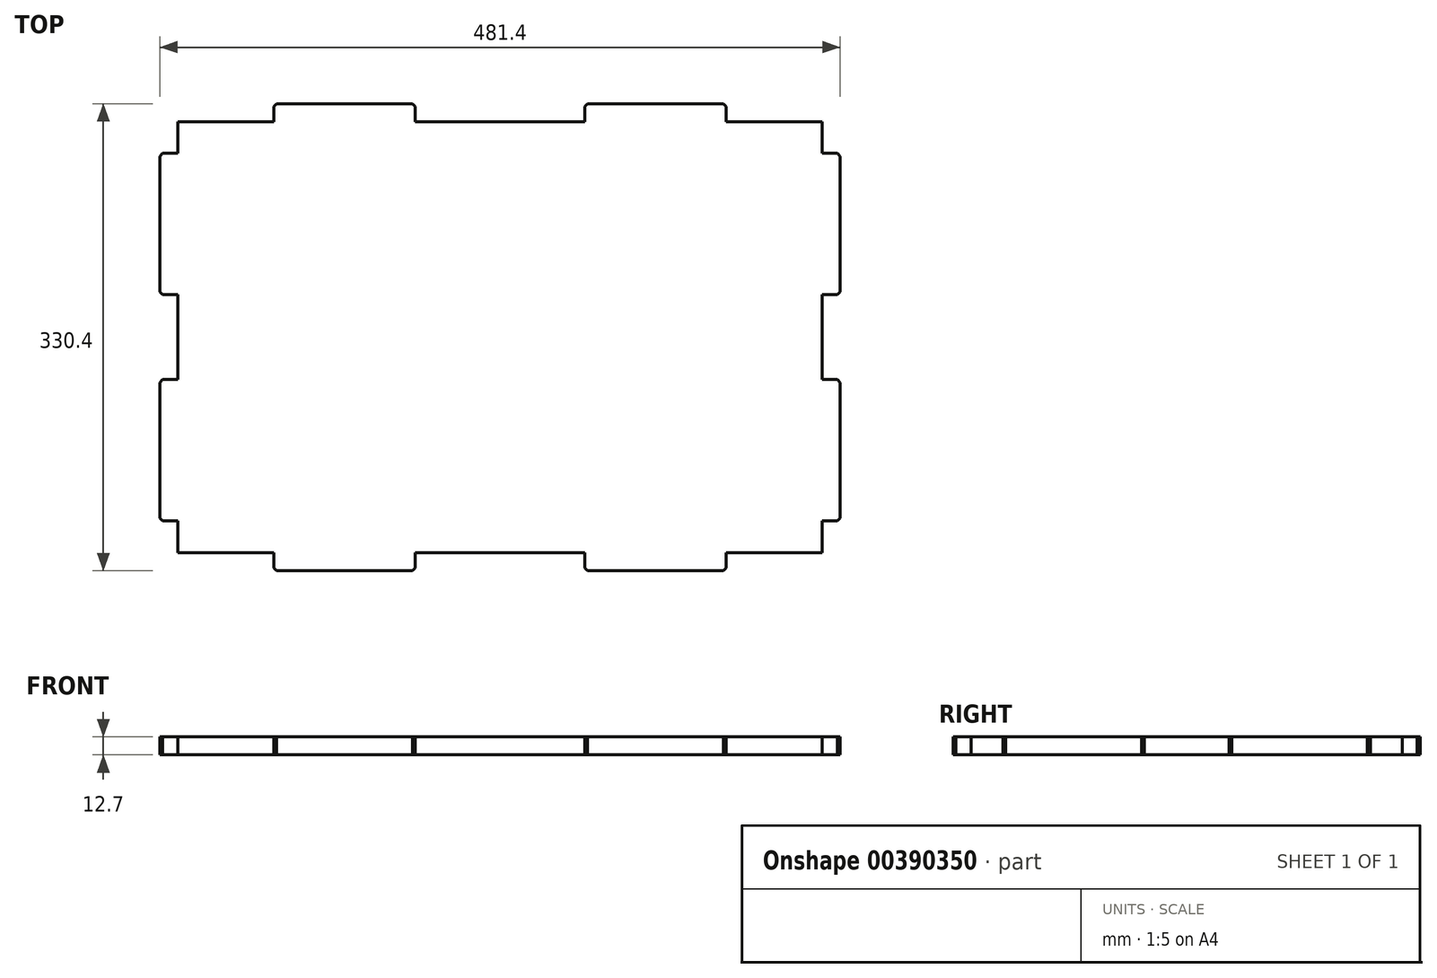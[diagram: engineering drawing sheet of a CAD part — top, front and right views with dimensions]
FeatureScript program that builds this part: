
annotation { "Feature Type Name" : "Feature", "Feature Type Description" : "" }
export const myFeature = defineFeature(function(context is Context, id is Id, definition is map)
    precondition{}
    {
        {
            var Q0;
            Q0=qCreatedBy(makeId("Top.planeOp"),FACE);
            var sketch = newSketch(context, id + "F0", { "sketchPlane" : qUnion([Q0])});
            skLineSegment(sketch, "E0.bottom", {"start": v(228, -152.5) * mm, "end": v(160, -152.5) * mm});
            skLineSegment(sketch, "E0.top", {"start": v(228, 152.5) * mm, "end": v(160, 152.5) * mm});
            skLineSegment(sketch, "E0.left", {"start": v(228, -152.5) * mm, "end": v(228, -130) * mm});
            skLineSegment(sketch, "E0.right", {"start": v(-228, -152.5) * mm, "end": v(-228, -130) * mm});
            skPoint(sketch, "E0.middle", {"position": v(0, 0) * mm});
            skLineSegment(sketch, "E1.bottom", {"start": v(-228, -30) * mm, "end": v(-240.7, -30) * mm});
            skLineSegment(sketch, "E1.top", {"start": v(-228, -130) * mm, "end": v(-240.7, -130) * mm});
            skLineSegment(sketch, "E1.right", {"start": v(-240.7, -30) * mm, "end": v(-240.7, -130) * mm});
            skLineSegment(sketch, "E2.trimOffspring", {"start": v(-228, -30) * mm, "end": v(-228, 30) * mm});
            skLineSegment(sketch, "E3.MirrorCS", {"start": v(-228, 30) * mm, "end": v(-240.7, 30) * mm});
            skLineSegment(sketch, "E4.MirrorCS", {"start": v(-228, 130) * mm, "end": v(-240.7, 130) * mm});
            skLineSegment(sketch, "E5.MirrorCS", {"start": v(-240.7, 30) * mm, "end": v(-240.7, 130) * mm});
            skLineSegment(sketch, "E6.MirrorCS", {"start": v(228, 130) * mm, "end": v(240.7, 130) * mm});
            skLineSegment(sketch, "E7.MirrorCS", {"start": v(240.7, 30) * mm, "end": v(240.7, 130) * mm});
            skLineSegment(sketch, "E8.MirrorCS", {"start": v(228, 30) * mm, "end": v(240.7, 30) * mm});
            skLineSegment(sketch, "E9.MirrorCS", {"start": v(228, -30) * mm, "end": v(240.7, -30) * mm});
            skLineSegment(sketch, "E10.MirrorCS", {"start": v(240.7, -30) * mm, "end": v(240.7, -130) * mm});
            skLineSegment(sketch, "E11.MirrorCS", {"start": v(228, -130) * mm, "end": v(240.7, -130) * mm});
            skLineSegment(sketch, "E12.trimOffspring", {"start": v(-228, 130) * mm, "end": v(-228, 152.5) * mm});
            skLineSegment(sketch, "E13.trimOffspring", {"start": v(228, 130) * mm, "end": v(228, 152.5) * mm});
            skLineSegment(sketch, "E14.trimOffspring", {"start": v(228, -30) * mm, "end": v(228, 30) * mm});
            skLineSegment(sketch, "E15.top", {"start": v(-160, 165.2) * mm, "end": v(-60, 165.2) * mm});
            skLineSegment(sketch, "E15.left", {"start": v(-160, 152.5) * mm, "end": v(-160, 165.2) * mm});
            skLineSegment(sketch, "E15.right", {"start": v(-60, 152.5) * mm, "end": v(-60, 165.2) * mm});
            skLineSegment(sketch, "E16.trimOffspring", {"start": v(-160, 152.5) * mm, "end": v(-228, 152.5) * mm});
            skLineSegment(sketch, "E17.MirrorCS", {"start": v(-60, -152.5) * mm, "end": v(-60, -165.2) * mm});
            skLineSegment(sketch, "E18.MirrorCS", {"start": v(-160, -152.5) * mm, "end": v(-160, -165.2) * mm});
            skLineSegment(sketch, "E19.MirrorCS", {"start": v(-160, -165.2) * mm, "end": v(-60, -165.2) * mm});
            skLineSegment(sketch, "E20.MirrorCS", {"start": v(160, 152.5) * mm, "end": v(160, 165.2) * mm});
            skLineSegment(sketch, "E21.MirrorCS", {"start": v(60, 152.5) * mm, "end": v(60, 165.2) * mm});
            skLineSegment(sketch, "E22.MirrorCS", {"start": v(160, 165.2) * mm, "end": v(60, 165.2) * mm});
            skLineSegment(sketch, "E23.MirrorCS", {"start": v(60, -152.5) * mm, "end": v(60, -165.2) * mm});
            skLineSegment(sketch, "E24.MirrorCS", {"start": v(160, -152.5) * mm, "end": v(160, -165.2) * mm});
            skLineSegment(sketch, "E25.MirrorCS", {"start": v(160, -165.2) * mm, "end": v(60, -165.2) * mm});
            skLineSegment(sketch, "E26.trimOffspring", {"start": v(60, 152.5) * mm, "end": v(-60, 152.5) * mm});
            skLineSegment(sketch, "E27.trimOffspring", {"start": v(60, -152.5) * mm, "end": v(-60, -152.5) * mm});
            skLineSegment(sketch, "E28.trimOffspring", {"start": v(-160, -152.5) * mm, "end": v(-228, -152.5) * mm});
            skSolve(sketch);
        }
        {
            var Q0;
            Q0 = qSketchRegion(id + "F0", true);
            extrude(context, id + "F1", {"entities" : qUnion([Q0]), "depth" : 12.7 * mm});
        }
        {
            var Q0;
            Q0=makeQuery(id+"F1.opExtrude","SWEPT_EDGE",EDGE,{"disambiguationData":[OSD([sQuery(id+"F0.wireOp",EDGE,"E20.MirrorCS"),sQuery(id+"F0.wireOp",EDGE,"E22.MirrorCS")])]});
            var Q1;
            Q1=makeQuery(id+"F1.opExtrude","SWEPT_EDGE",EDGE,{"disambiguationData":[OSD([sQuery(id+"F0.wireOp",EDGE,"E6.MirrorCS"),sQuery(id+"F0.wireOp",EDGE,"E7.MirrorCS")])]});
            var Q2;
            Q2=makeQuery(id+"F1.opExtrude","SWEPT_EDGE",EDGE,{"disambiguationData":[OSD([sQuery(id+"F0.wireOp",EDGE,"E7.MirrorCS"),sQuery(id+"F0.wireOp",EDGE,"E8.MirrorCS")])]});
            var Q3;
            Q3=makeQuery(id+"F1.opExtrude","SWEPT_EDGE",EDGE,{"disambiguationData":[OSD([sQuery(id+"F0.wireOp",EDGE,"E9.MirrorCS"),sQuery(id+"F0.wireOp",EDGE,"E10.MirrorCS")])]});
            var Q4;
            Q4=makeQuery(id+"F1.opExtrude","SWEPT_EDGE",EDGE,{"disambiguationData":[OSD([sQuery(id+"F0.wireOp",EDGE,"E10.MirrorCS"),sQuery(id+"F0.wireOp",EDGE,"E11.MirrorCS")])]});
            var Q5;
            Q5=makeQuery(id+"F1.opExtrude","SWEPT_EDGE",EDGE,{"disambiguationData":[OSD([sQuery(id+"F0.wireOp",EDGE,"E24.MirrorCS"),sQuery(id+"F0.wireOp",EDGE,"E25.MirrorCS")])]});
            var Q6;
            Q6=makeQuery(id+"F1.opExtrude","SWEPT_EDGE",EDGE,{"disambiguationData":[OSD([sQuery(id+"F0.wireOp",EDGE,"E15.top"),sQuery(id+"F0.wireOp",EDGE,"E15.right")])]});
            var Q7;
            Q7=makeQuery(id+"F1.opExtrude","SWEPT_EDGE",EDGE,{"disambiguationData":[OSD([sQuery(id+"F0.wireOp",EDGE,"E21.MirrorCS"),sQuery(id+"F0.wireOp",EDGE,"E22.MirrorCS")])]});
            var Q8;
            Q8=makeQuery(id+"F1.opExtrude","SWEPT_EDGE",EDGE,{"disambiguationData":[OSD([sQuery(id+"F0.wireOp",EDGE,"E15.top"),sQuery(id+"F0.wireOp",EDGE,"E15.left")])]});
            var Q9;
            Q9=makeQuery(id+"F1.opExtrude","SWEPT_EDGE",EDGE,{"disambiguationData":[OSD([sQuery(id+"F0.wireOp",EDGE,"E23.MirrorCS"),sQuery(id+"F0.wireOp",EDGE,"E25.MirrorCS")])]});
            var Q10;
            Q10=makeQuery(id+"F1.opExtrude","SWEPT_EDGE",EDGE,{"disambiguationData":[OSD([sQuery(id+"F0.wireOp",EDGE,"E17.MirrorCS"),sQuery(id+"F0.wireOp",EDGE,"E19.MirrorCS")])]});
            var Q11;
            Q11=makeQuery(id+"F1.opExtrude","SWEPT_EDGE",EDGE,{"disambiguationData":[OSD([sQuery(id+"F0.wireOp",EDGE,"E18.MirrorCS"),sQuery(id+"F0.wireOp",EDGE,"E19.MirrorCS")])]});
            var Q12;
            Q12=makeQuery(id+"F1.opExtrude","SWEPT_EDGE",EDGE,{"disambiguationData":[OSD([sQuery(id+"F0.wireOp",EDGE,"E1.top"),sQuery(id+"F0.wireOp",EDGE,"E1.right")])]});
            var Q13;
            Q13=makeQuery(id+"F1.opExtrude","SWEPT_EDGE",EDGE,{"disambiguationData":[OSD([sQuery(id+"F0.wireOp",EDGE,"E1.bottom"),sQuery(id+"F0.wireOp",EDGE,"E1.right")])]});
            var Q14;
            Q14=makeQuery(id+"F1.opExtrude","SWEPT_EDGE",EDGE,{"disambiguationData":[OSD([sQuery(id+"F0.wireOp",EDGE,"E3.MirrorCS"),sQuery(id+"F0.wireOp",EDGE,"E5.MirrorCS")])]});
            var Q15;
            Q15=makeQuery(id+"F1.opExtrude","SWEPT_EDGE",EDGE,{"disambiguationData":[OSD([sQuery(id+"F0.wireOp",EDGE,"E4.MirrorCS"),sQuery(id+"F0.wireOp",EDGE,"E5.MirrorCS")])]});
            chamfer(context, id + "F2", {"entities" : qUnion([Q0, Q1, Q2, Q3, Q4, Q5, Q6, Q7, Q8, Q9, Q10, Q11, Q12, Q13, Q14, Q15]), "width" : 2 * mm, "tangentPropagation" : true});
        }
    });
